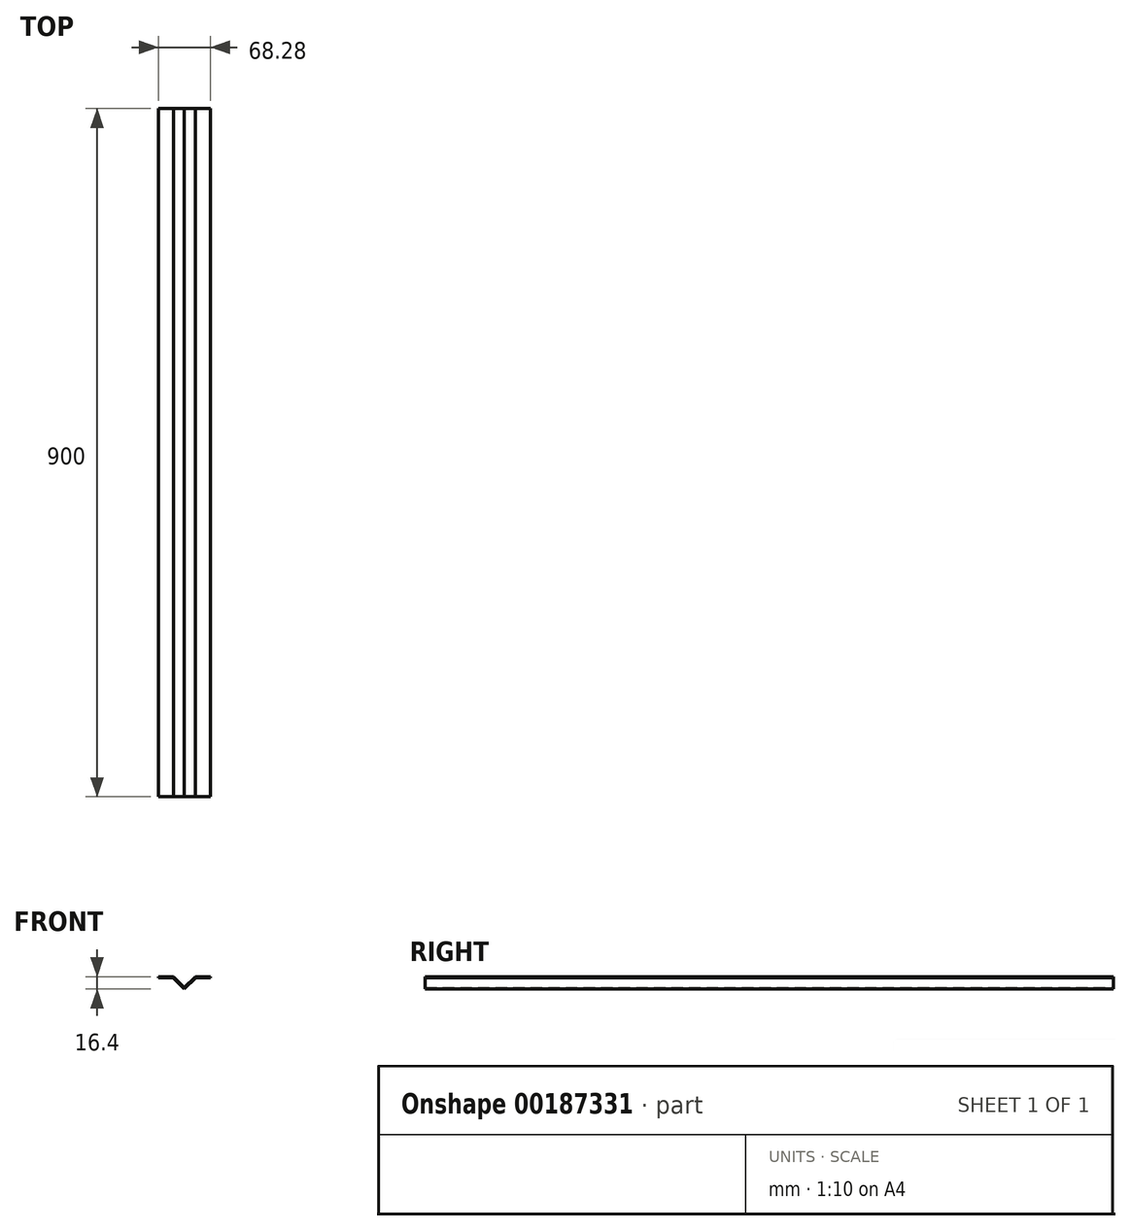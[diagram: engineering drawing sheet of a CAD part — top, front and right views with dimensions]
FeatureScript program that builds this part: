
annotation { "Feature Type Name" : "Feature", "Feature Type Description" : "" }
export const myFeature = defineFeature(function(context is Context, id is Id, definition is map)
    precondition{}
    {
        {
            var Q0;
            Q0=qCreatedBy(makeId("Front.planeOp"),FACE);
            var sketch = newSketch(context, id + "F0", { "sketchPlane" : qUnion([Q0])});
            skLineSegment(sketch, "E0", {"start": v(-34.14, 0) * mm, "end": v(-14.14, 0) * mm});
            skLineSegment(sketch, "E1", {"start": v(14.14, 0) * mm, "end": v(34.14, 0) * mm});
            skLineSegment(sketch, "E2", {"start": v(-14.14, 0) * mm, "end": v(0, -14.14) * mm});
            skLineSegment(sketch, "E3", {"start": v(0, -14.14) * mm, "end": v(14.14, 0) * mm});
            skLineSegment(sketch, "E4.0", {"start": v(14.8, -1.6) * mm, "end": v(34.14, -1.6) * mm});
            skLineSegment(sketch, "E4.1", {"start": v(0, -16.4) * mm, "end": v(14.8, -1.6) * mm});
            skLineSegment(sketch, "E4.2", {"start": v(-14.8, -1.6) * mm, "end": v(0, -16.4) * mm});
            skLineSegment(sketch, "E4.3", {"start": v(-34.14, -1.6) * mm, "end": v(-14.8, -1.6) * mm});
            skLineSegment(sketch, "E5", {"start": v(-34.14, 0) * mm, "end": v(-34.14, -1.6) * mm});
            skLineSegment(sketch, "E6", {"start": v(34.14, 0) * mm, "end": v(34.14, -1.6) * mm});
            skSolve(sketch);
        }
        {
            var Q0;
            Q0=qSketchRegion(id+"F0",true);
            extrude(context, id + "F1", {"entities" : qUnion([Q0]), "endBound" : BoundingType.SYMMETRIC, "depth" : 900 * mm});
        }
    });
